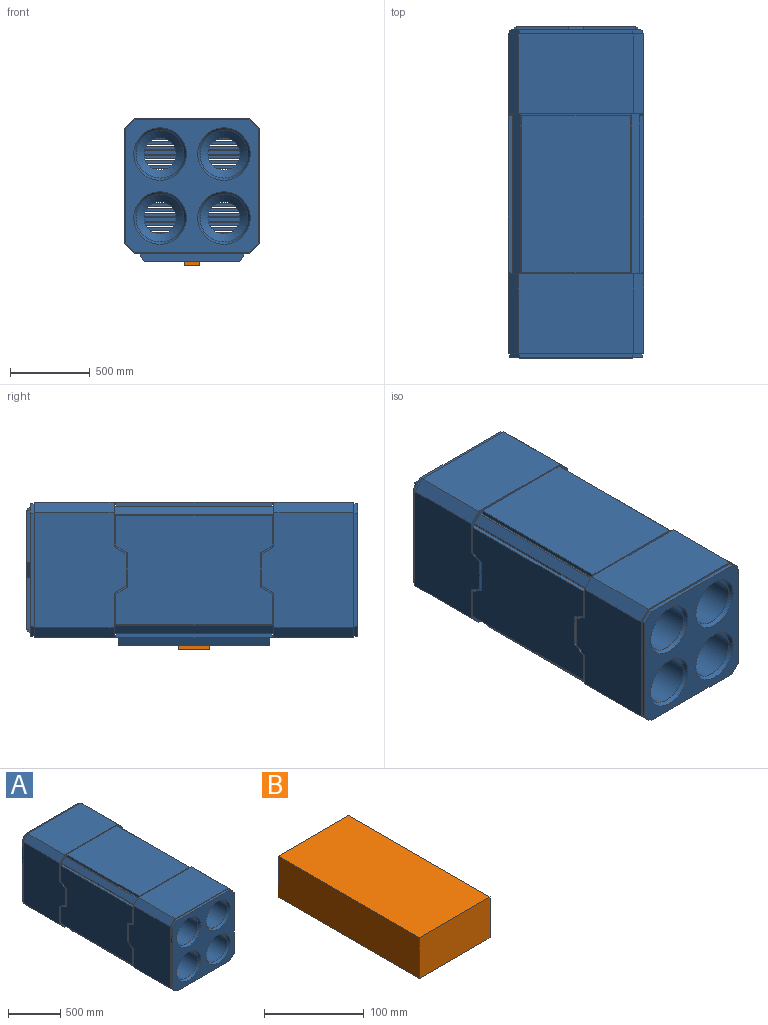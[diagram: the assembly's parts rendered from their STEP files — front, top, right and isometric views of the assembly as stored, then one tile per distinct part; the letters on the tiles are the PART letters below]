
ASSEMBLY  parts=2 mates=1
PART A: 237 faces, bbox 850x2075x900 mm
  f0: plane 950x600mm, normal (0,0,-1), area 550000mm2, adj f155,f156,f157,f231,f232,f233,f234,f235
  f1: plane 980x680mm, normal (0,0,-1), area 41551.7mm2, adj f32,f33,f34,f155,f156,f157,f171,f231
  f2: plane 850x280.77mm, normal (0,-1,0), area 32359.7mm2, adj f4,f13,f15,f22,f23,f24,f141,f158
  f3: plane 850x280.77mm, normal (0,1,0), area 32359.7mm2, adj f4,f12,f14,f16,f17,f18,f139,f158
  f4: plane 1000x700mm, normal (1,0,0), area 35332.1mm2, adj f2,f3,f5,f6,f14,f15,f21,f27
  f5: plane 190x25mm, normal (0,-1,0), area 4750mm2, adj f4,f7,f37,f136
  f6: plane 190x25mm, normal (0,1,0), area 4750mm2, adj f4,f7,f37,f132
  f7: plane 980x680mm, normal (1,0,0), area 627895.2mm2, adj f5,f6,f35,f36,f37,f38,f132,f133
  f8: plane 830x830mm, normal (0,1,0), area 111488.2mm2, adj f45,f46,f47,f48,f49,f50,f51,f52
  f9: plane 750x750mm, normal (0,1,0), area 394500mm2, adj f50,f51,f52,f53,f54,f55,f56,f57
  f10: plane 850x850mm, normal (0,1,0), area 32153.9mm2, adj f22,f23,f24,f25,f26,f45,f46,f47
  f11: plane 850x850mm, normal (0,-1,0), area 32153.9mm2, adj f16,f17,f18,f19,f20,f39,f40,f41
  f12: plane 1000x700mm, normal (0,0,-1), area 33600mm2, adj f3,f14,f27,f32,f33,f34,f162,f171
  f13: plane 1000x700mm, normal (0,0,1), area 33600mm2, adj f2,f15,f21,f28,f29,f30,f163,f170
  f14: plane 1000x50mm, normal (0.71,0,-0.71), area 70710.7mm2, adj f3,f4,f12,f27
  f15: plane 1000x50mm, normal (0.71,0,0.71), area 70710.7mm2, adj f2,f4,f13,f21
  f16: plane 720.71x500mm, normal (0,0,-1), area 360355.3mm2, adj f3,f11,f17,f164
  f17: plane 500x64.64mm, normal (0.71,0,-0.71), area 45710.7mm2, adj f3,f11,f16,f18
  f18: plane 720.71x575mm, normal (1,0,0), area 378741.7mm2, adj f3,f11,f17,f19,f21,f138,f139,f140
  f19: plane 500x64.64mm, normal (0.71,0,0.71), area 45710.7mm2, adj f11,f18,f20,f21
  f20: plane 720.71x500mm, normal (0,0,1), area 360355.3mm2, adj f11,f19,f21,f166
  f21: plane 850x280.77mm, normal (0,1,0), area 32359.7mm2, adj f4,f13,f15,f18,f19,f20,f138,f158
  f22: plane 720.71x500mm, normal (0,0,1), area 360355.3mm2, adj f2,f10,f23,f167
  f23: plane 500x64.64mm, normal (0.71,0,0.71), area 45710.7mm2, adj f2,f10,f22,f24
  f24: plane 720.71x575mm, normal (1,0,0), area 378741.7mm2, adj f2,f10,f23,f25,f27,f141,f142,f143
  f25: plane 500x64.64mm, normal (0.71,0,-0.71), area 45710.7mm2, adj f10,f24,f26,f27
  f26: plane 720.71x500mm, normal (0,0,-1), area 360355.3mm2, adj f10,f25,f27,f169
  f27: plane 850x280.77mm, normal (0,-1,0), area 32359.7mm2, adj f4,f12,f14,f24,f25,f26,f143,f158
  f28: plane 680x25mm, normal (0,1,0), area 17000mm2, adj f13,f30,f31,f170
  f29: plane 680x25mm, normal (0,-1,0), area 17000mm2, adj f13,f30,f31,f170
  f30: plane 980x25mm, normal (1,0,0), area 24500mm2, adj f13,f28,f29,f31
  f31: plane 980x680mm, normal (0,0,1), area 666400mm2, adj f28,f29,f30,f170
  f32: plane 680x25mm, normal (0,-1,0), area 17000mm2, adj f1,f12,f34,f171
  f33: plane 680x25mm, normal (0,1,0), area 17000mm2, adj f1,f12,f34,f171
  f34: plane 980x25mm, normal (1,0,0), area 24500mm2, adj f1,f12,f32,f33
  f35: plane 980x25mm, normal (0,0,1), area 24500mm2, adj f4,f7,f36,f38
  f36: plane 190x25mm, normal (0,-1,0), area 4750mm2, adj f4,f7,f35,f135
  f37: plane 980x25mm, normal (0,0,-1), area 24500mm2, adj f4,f5,f6,f7
  f38: plane 190x25mm, normal (0,1,0), area 4750mm2, adj f4,f7,f35,f133
  f39: plane 712.43x25mm, normal (0,0,1), area 17810.7mm2, adj f11,f43,f44,f178
  f40: plane 712.43x25mm, normal (0,0,-1), area 17810.7mm2, adj f11,f41,f44,f176
  f41: plane 58.79x58.79mm, normal (0.71,0,-0.71), area 2078.4mm2, adj f11,f40,f42,f44
  f42: plane 712.43x25mm, normal (1,0,0), area 17810.7mm2, adj f11,f41,f43,f44
  f43: plane 58.79x58.79mm, normal (0.71,0,0.71), area 2078.4mm2, adj f11,f39,f42,f44
  f44: plane 830x830mm, normal (0,-1,0), area 342212.9mm2, adj f39,f40,f41,f42,f43,f146,f147,f176
  f45: plane 712.43x25mm, normal (0,0,1), area 17810.7mm2, adj f8,f10,f46,f179
  f46: plane 58.79x58.79mm, normal (0.71,0,0.71), area 2078.4mm2, adj f8,f10,f45,f47
  f47: plane 712.43x25mm, normal (1,0,0), area 17810.7mm2, adj f8,f10,f46,f48
  f48: plane 58.79x58.79mm, normal (0.71,0,-0.71), area 2078.4mm2, adj f8,f10,f47,f49
  f49: plane 712.43x25mm, normal (0,0,-1), area 17810.7mm2, adj f8,f10,f48,f181
  f50: plane 750x25mm, normal (0,0,-1), area 16750mm2, adj f8,f9,f52,f128,f131,f182,f210
  f51: plane 750x25mm, normal (0,0,1), area 16750mm2, adj f8,f9,f52,f125,f129,f182,f207
  f52: plane 750x25mm, normal (1,0,0), area 16750mm2, adj f8,f9,f50,f51,f126,f127,f130
  f53: plane 700x25mm, normal (0,0,1), area 17500mm2, adj f9,f55,f154,f183
  f54: plane 700x25mm, normal (0,0,-1), area 17500mm2, adj f9,f55,f154,f183
  f55: plane 25x10mm, normal (-1,0,0), area 250mm2, adj f9,f53,f54,f154
  f56: plane 700x25mm, normal (0,0,1), area 17500mm2, adj f9,f58,f154,f184
  f57: plane 700x25mm, normal (0,0,-1), area 17500mm2, adj f9,f58,f154,f184
  f58: plane 25x10mm, normal (-1,0,0), area 250mm2, adj f9,f56,f57,f154
  f59: plane 700x25mm, normal (0,0,1), area 17500mm2, adj f9,f61,f154,f185
  f60: plane 700x25mm, normal (0,0,-1), area 17500mm2, adj f9,f61,f154,f185
  f61: plane 25x10mm, normal (-1,0,0), area 250mm2, adj f9,f59,f60,f154
  f62: plane 700x25mm, normal (0,0,1), area 17500mm2, adj f9,f64,f154,f186
  f63: plane 700x25mm, normal (0,0,-1), area 17500mm2, adj f9,f64,f154,f186
  f64: plane 25x10mm, normal (-1,0,0), area 250mm2, adj f9,f62,f63,f154
  f65: plane 700x25mm, normal (0,0,1), area 17500mm2, adj f9,f67,f154,f187
  f66: plane 700x25mm, normal (0,0,-1), area 17500mm2, adj f9,f67,f154,f187
  f67: plane 25x10mm, normal (-1,0,0), area 250mm2, adj f9,f65,f66,f154
  f68: plane 700x25mm, normal (0,0,1), area 17500mm2, adj f9,f70,f154,f188
  f69: plane 700x25mm, normal (0,0,-1), area 17500mm2, adj f9,f70,f154,f188
  f70: plane 25x10mm, normal (-1,0,0), area 250mm2, adj f9,f68,f69,f154
  f71: plane 700x25mm, normal (0,0,1), area 17500mm2, adj f9,f73,f154,f189
  f72: plane 700x25mm, normal (0,0,-1), area 17500mm2, adj f9,f73,f154,f189
  f73: plane 25x10mm, normal (-1,0,0), area 250mm2, adj f9,f71,f72,f154
  f74: plane 700x25mm, normal (0,0,1), area 17500mm2, adj f9,f76,f154,f190
  f75: plane 700x25mm, normal (0,0,-1), area 17500mm2, adj f9,f76,f154,f190
  f76: plane 25x10mm, normal (-1,0,0), area 250mm2, adj f9,f74,f75,f154
  f77: plane 700x25mm, normal (0,0,1), area 17500mm2, adj f9,f79,f154,f191
  f78: plane 700x25mm, normal (0,0,-1), area 17500mm2, adj f9,f79,f154,f191
  f79: plane 25x10mm, normal (-1,0,0), area 250mm2, adj f9,f77,f78,f154
  f80: plane 700x25mm, normal (0,0,1), area 17500mm2, adj f9,f82,f154,f192
  f81: plane 700x25mm, normal (0,0,-1), area 17500mm2, adj f9,f82,f154,f192
  f82: plane 25x10mm, normal (-1,0,0), area 250mm2, adj f9,f80,f81,f154
  f83: plane 700x25mm, normal (0,0,1), area 17500mm2, adj f9,f85,f154,f193
  f84: plane 700x25mm, normal (0,0,-1), area 17500mm2, adj f9,f85,f154,f193
  f85: plane 25x10mm, normal (-1,0,0), area 250mm2, adj f9,f83,f84,f154
  f86: plane 700x25mm, normal (0,0,1), area 17500mm2, adj f9,f88,f154,f194
  f87: plane 700x25mm, normal (0,0,-1), area 17500mm2, adj f9,f88,f154,f194
  f88: plane 25x10mm, normal (-1,0,0), area 250mm2, adj f9,f86,f87,f154
  f89: plane 700x25mm, normal (0,0,1), area 17500mm2, adj f9,f91,f154,f195
  f90: plane 700x25mm, normal (0,0,-1), area 17500mm2, adj f9,f91,f154,f195
  f91: plane 25x10mm, normal (-1,0,0), area 250mm2, adj f9,f89,f90,f154
  f92: plane 700x25mm, normal (0,0,1), area 17500mm2, adj f9,f94,f154,f196
  f93: plane 700x25mm, normal (0,0,-1), area 17500mm2, adj f9,f94,f154,f196
  f94: plane 25x10mm, normal (-1,0,0), area 250mm2, adj f9,f92,f93,f154
  f95: plane 700x25mm, normal (0,0,1), area 17500mm2, adj f9,f97,f154,f197
  f96: plane 700x25mm, normal (0,0,-1), area 17500mm2, adj f9,f97,f154,f197
  f97: plane 25x10mm, normal (-1,0,0), area 250mm2, adj f9,f95,f96,f154
  f98: plane 700x25mm, normal (0,0,1), area 17500mm2, adj f9,f100,f154,f198
  f99: plane 700x25mm, normal (0,0,-1), area 17500mm2, adj f9,f100,f154,f198
  f100: plane 25x10mm, normal (-1,0,0), area 250mm2, adj f9,f98,f99,f154
  f101: plane 700x25mm, normal (0,0,1), area 17500mm2, adj f9,f103,f154,f199
  f102: plane 700x25mm, normal (0,0,-1), area 17500mm2, adj f9,f103,f154,f199
  f103: plane 25x10mm, normal (-1,0,0), area 250mm2, adj f9,f101,f102,f154
  f104: plane 700x25mm, normal (0,0,1), area 17500mm2, adj f9,f106,f154,f200
  f105: plane 700x25mm, normal (0,0,-1), area 17500mm2, adj f9,f106,f154,f200
  f106: plane 25x10mm, normal (-1,0,0), area 250mm2, adj f9,f104,f105,f154
  f107: plane 700x25mm, normal (0,0,1), area 17500mm2, adj f9,f109,f154,f201
  f108: plane 700x25mm, normal (0,0,-1), area 17500mm2, adj f9,f109,f154,f201
  f109: plane 25x10mm, normal (-1,0,0), area 250mm2, adj f9,f107,f108,f154
  f110: plane 700x25mm, normal (0,0,1), area 17500mm2, adj f9,f112,f154,f202
  f111: plane 700x25mm, normal (0,0,-1), area 17500mm2, adj f9,f112,f154,f202
  f112: plane 25x10mm, normal (-1,0,0), area 250mm2, adj f9,f110,f111,f154
  f113: plane 700x25mm, normal (0,0,1), area 17500mm2, adj f9,f115,f154,f203
  f114: plane 700x25mm, normal (0,0,-1), area 17500mm2, adj f9,f115,f154,f203
  f115: plane 25x10mm, normal (-1,0,0), area 250mm2, adj f9,f113,f114,f154
  f116: plane 700x25mm, normal (0,0,1), area 17500mm2, adj f9,f118,f154,f204
  f117: plane 700x25mm, normal (0,0,-1), area 17500mm2, adj f9,f118,f154,f204
  f118: plane 25x10mm, normal (-1,0,0), area 250mm2, adj f9,f116,f117,f154
  f119: plane 700x25mm, normal (0,0,1), area 17500mm2, adj f9,f121,f154,f205
  f120: plane 700x25mm, normal (0,0,-1), area 17500mm2, adj f9,f121,f154,f205
  f121: plane 25x10mm, normal (-1,0,0), area 250mm2, adj f9,f119,f120,f154
  f122: plane 700x25mm, normal (0,0,1), area 17500mm2, adj f9,f124,f154,f206
  f123: plane 700x25mm, normal (0,0,-1), area 17500mm2, adj f9,f124,f154,f206
  f124: plane 25x10mm, normal (-1,0,0), area 250mm2, adj f9,f122,f123,f154
  f125: plane 20x20mm, normal (1,0,0), area 200mm2, adj f8,f51,f129
  f126: plane 20x20mm, normal (0,0,1), area 200mm2, adj f8,f52,f130
  f127: plane 20x20mm, normal (0,0,-1), area 200mm2, adj f8,f52,f130
  f128: plane 20x20mm, normal (1,0,0), area 200mm2, adj f8,f50,f131
  f129: plane 100x20mm, normal (0,0.71,0.71), area 2828.4mm2, adj f8,f51,f125,f207
  f130: plane 100x20mm, normal (0.71,0.71,0), area 2828.4mm2, adj f8,f52,f126,f127
  f131: plane 100x20mm, normal (0,0.71,-0.71), area 2828.4mm2, adj f8,f50,f128,f210
  f132: plane 75x43.3mm, normal (0,0.5,0.87), area 2165.1mm2, adj f4,f6,f7,f134
  f133: plane 75x43.3mm, normal (0,0.5,-0.87), area 2165.1mm2, adj f4,f7,f38,f134
  f134: plane 213.4x25mm, normal (0,1,0), area 5334.9mm2, adj f4,f7,f132,f133
  f135: plane 75x43.3mm, normal (0,-0.5,-0.87), area 2165.1mm2, adj f4,f7,f36,f137
  f136: plane 75x43.3mm, normal (0,-0.5,0.87), area 2165.1mm2, adj f4,f5,f7,f137
  f137: plane 213.4x25mm, normal (0,-1,0), area 5334.9mm2, adj f4,f7,f135,f136
  f138: plane 75x43.3mm, normal (0,0.5,0.87), area 2165.1mm2, adj f4,f18,f21,f140
  f139: plane 75x43.3mm, normal (0,0.5,-0.87), area 2165.1mm2, adj f3,f4,f18,f140
  f140: plane 201.85x25mm, normal (0,1,0), area 5046.3mm2, adj f4,f18,f138,f139
  f141: plane 75x43.3mm, normal (0,-0.5,0.87), area 2165.1mm2, adj f2,f4,f24,f142
  f142: plane 201.85x25mm, normal (0,-1,0), area 5046.3mm2, adj f4,f24,f141,f143
  f143: plane 75x43.3mm, normal (0,-0.5,-0.87), area 2165.1mm2, adj f4,f24,f27,f142
  f144: cylinder r=150mm len=1925mm, axis (0,-1,0), area 1814269.8mm2, adj f146,f148
  f145: cylinder r=150mm len=1925mm, axis (0,-1,0), area 1814269.8mm2, adj f147,f149
  f146: cone r=150mm half-angle=30deg, axis (0,-1,0), area 28516mm2, adj f44,f144
  f147: cone r=150mm half-angle=30deg, axis (0,-1,0), area 28516mm2, adj f44,f145
  f148: cone r=100mm half-angle=45deg, axis (0,-1,0), area 55536mm2, adj f144,f150
  f149: cone r=100mm half-angle=45deg, axis (0,-1,0), area 55536mm2, adj f145,f150
  f150: plane 720x720mm, normal (0,1,0), area 392736.3mm2, adj f148,f149,f151,f152,f153,f228,f229,f230
  f151: plane 720x50mm, normal (0,0,-1), area 36000mm2, adj f150,f152,f154,f230
  f152: plane 720x50mm, normal (-1,0,0), area 36000mm2, adj f150,f151,f153,f154
  f153: plane 720x50mm, normal (0,0,1), area 36000mm2, adj f150,f152,f154,f230
  f154: plane 720x720mm, normal (0,-1,0), area 350400mm2, adj f53,f54,f55,f56,f57,f58,f59,f60
  f155: plane 657.74x50mm, normal (0,-1,0), area 31443.4mm2, adj f0,f1,f157,f231
  f156: plane 657.74x50mm, normal (0,1,0), area 31443.4mm2, adj f0,f1,f157,f231
  f157: plane 950x50mm, normal (0.87,0,-0.5), area 54848.3mm2, adj f0,f1,f155,f156
  f158: plane 1000x700mm, normal (-1,0,0), area 35332.1mm2, adj f2,f3,f21,f27,f159,f160,f162,f163
  f159: plane 190x25mm, normal (0,-1,0), area 4750mm2, adj f158,f161,f174,f216
  f160: plane 190x25mm, normal (0,1,0), area 4750mm2, adj f158,f161,f174,f212
  f161: plane 980x680mm, normal (-1,0,0), area 627895.2mm2, adj f159,f160,f172,f173,f174,f175,f212,f213
  f162: plane 1000x50mm, normal (-0.71,0,-0.71), area 70710.7mm2, adj f3,f12,f27,f158
  f163: plane 1000x50mm, normal (-0.71,0,0.71), area 70710.7mm2, adj f2,f13,f21,f158
  f164: plane 500x64.64mm, normal (-0.71,0,-0.71), area 45710.7mm2, adj f3,f11,f16,f165
  f165: plane 720.71x575mm, normal (-1,0,0), area 378741.7mm2, adj f3,f11,f21,f164,f166,f218,f219,f220
  f166: plane 500x64.64mm, normal (-0.71,0,0.71), area 45710.7mm2, adj f11,f20,f21,f165
  f167: plane 500x64.64mm, normal (-0.71,0,0.71), area 45710.7mm2, adj f2,f10,f22,f168
  f168: plane 720.71x575mm, normal (-1,0,0), area 378741.7mm2, adj f2,f10,f27,f167,f169,f221,f222,f223
  f169: plane 500x64.64mm, normal (-0.71,0,-0.71), area 45710.7mm2, adj f10,f26,f27,f168
  f170: plane 980x25mm, normal (-1,0,0), area 24500mm2, adj f13,f28,f29,f31
  f171: plane 980x25mm, normal (-1,0,0), area 24500mm2, adj f1,f12,f32,f33
  f172: plane 980x25mm, normal (0,0,1), area 24500mm2, adj f158,f161,f173,f175
  f173: plane 190x25mm, normal (0,-1,0), area 4750mm2, adj f158,f161,f172,f215
  f174: plane 980x25mm, normal (0,0,-1), area 24500mm2, adj f158,f159,f160,f161
  f175: plane 190x25mm, normal (0,1,0), area 4750mm2, adj f158,f161,f172,f213
  f176: plane 58.79x58.79mm, normal (-0.71,0,-0.71), area 2078.4mm2, adj f11,f40,f44,f177
  f177: plane 712.43x25mm, normal (-1,0,0), area 17810.7mm2, adj f11,f44,f176,f178
  f178: plane 58.79x58.79mm, normal (-0.71,0,0.71), area 2078.4mm2, adj f11,f39,f44,f177
  f179: plane 58.79x58.79mm, normal (-0.71,0,0.71), area 2078.4mm2, adj f8,f10,f45,f180
  f180: plane 712.43x25mm, normal (-1,0,0), area 17810.7mm2, adj f8,f10,f179,f181
  f181: plane 58.79x58.79mm, normal (-0.71,0,-0.71), area 2078.4mm2, adj f8,f10,f49,f180
  f182: plane 750x25mm, normal (-1,0,0), area 16750mm2, adj f8,f9,f50,f51,f208,f209,f211
  f183: plane 25x10mm, normal (1,0,0), area 250mm2, adj f9,f53,f54,f154
  f184: plane 25x10mm, normal (1,0,0), area 250mm2, adj f9,f56,f57,f154
  f185: plane 25x10mm, normal (1,0,0), area 250mm2, adj f9,f59,f60,f154
  f186: plane 25x10mm, normal (1,0,0), area 250mm2, adj f9,f62,f63,f154
  f187: plane 25x10mm, normal (1,0,0), area 250mm2, adj f9,f65,f66,f154
  f188: plane 25x10mm, normal (1,0,0), area 250mm2, adj f9,f68,f69,f154
  f189: plane 25x10mm, normal (1,0,0), area 250mm2, adj f9,f71,f72,f154
  f190: plane 25x10mm, normal (1,0,0), area 250mm2, adj f9,f74,f75,f154
  f191: plane 25x10mm, normal (1,0,0), area 250mm2, adj f9,f77,f78,f154
  f192: plane 25x10mm, normal (1,0,0), area 250mm2, adj f9,f80,f81,f154
  f193: plane 25x10mm, normal (1,0,0), area 250mm2, adj f9,f83,f84,f154
  f194: plane 25x10mm, normal (1,0,0), area 250mm2, adj f9,f86,f87,f154
  f195: plane 25x10mm, normal (1,0,0), area 250mm2, adj f9,f89,f90,f154
  f196: plane 25x10mm, normal (1,0,0), area 250mm2, adj f9,f92,f93,f154
  f197: plane 25x10mm, normal (1,0,0), area 250mm2, adj f9,f95,f96,f154
  f198: plane 25x10mm, normal (1,0,0), area 250mm2, adj f9,f98,f99,f154
  f199: plane 25x10mm, normal (1,0,0), area 250mm2, adj f9,f101,f102,f154
  f200: plane 25x10mm, normal (1,0,0), area 250mm2, adj f9,f104,f105,f154
  f201: plane 25x10mm, normal (1,0,0), area 250mm2, adj f9,f107,f108,f154
  f202: plane 25x10mm, normal (1,0,0), area 250mm2, adj f9,f110,f111,f154
  f203: plane 25x10mm, normal (1,0,0), area 250mm2, adj f9,f113,f114,f154
  f204: plane 25x10mm, normal (1,0,0), area 250mm2, adj f9,f116,f117,f154
  f205: plane 25x10mm, normal (1,0,0), area 250mm2, adj f9,f119,f120,f154
  f206: plane 25x10mm, normal (1,0,0), area 250mm2, adj f9,f122,f123,f154
  f207: plane 20x20mm, normal (-1,0,0), area 200mm2, adj f8,f51,f129
  f208: plane 20x20mm, normal (0,0,1), area 200mm2, adj f8,f182,f211
  f209: plane 20x20mm, normal (0,0,-1), area 200mm2, adj f8,f182,f211
  f210: plane 20x20mm, normal (-1,0,0), area 200mm2, adj f8,f50,f131
  f211: plane 100x20mm, normal (-0.71,0.71,0), area 2828.4mm2, adj f8,f182,f208,f209
  f212: plane 75x43.3mm, normal (0,0.5,0.87), area 2165.1mm2, adj f158,f160,f161,f214
  f213: plane 75x43.3mm, normal (0,0.5,-0.87), area 2165.1mm2, adj f158,f161,f175,f214
  f214: plane 213.4x25mm, normal (0,1,0), area 5334.9mm2, adj f158,f161,f212,f213
  f215: plane 75x43.3mm, normal (0,-0.5,-0.87), area 2165.1mm2, adj f158,f161,f173,f217
  f216: plane 75x43.3mm, normal (0,-0.5,0.87), area 2165.1mm2, adj f158,f159,f161,f217
  f217: plane 213.4x25mm, normal (0,-1,0), area 5334.9mm2, adj f158,f161,f215,f216
  f218: plane 75x43.3mm, normal (0,0.5,0.87), area 2165.1mm2, adj f21,f158,f165,f220
  f219: plane 75x43.3mm, normal (0,0.5,-0.87), area 2165.1mm2, adj f3,f158,f165,f220
  f220: plane 201.85x25mm, normal (0,1,0), area 5046.3mm2, adj f158,f165,f218,f219
  f221: plane 75x43.3mm, normal (0,-0.5,0.87), area 2165.1mm2, adj f2,f158,f168,f222
  f222: plane 201.85x25mm, normal (0,-1,0), area 5046.3mm2, adj f158,f168,f221,f223
  f223: plane 75x43.3mm, normal (0,-0.5,-0.87), area 2165.1mm2, adj f27,f158,f168,f222
  f224: cylinder r=150mm len=1925mm, axis (0,-1,0), area 1814269.8mm2, adj f226,f228
  f225: cylinder r=150mm len=1925mm, axis (0,-1,0), area 1814269.8mm2, adj f227,f229
  f226: cone r=150mm half-angle=30deg, axis (0,-1,0), area 28516mm2, adj f44,f224
  f227: cone r=150mm half-angle=30deg, axis (0,-1,0), area 28516mm2, adj f44,f225
  f228: cone r=100mm half-angle=45deg, axis (0,-1,0), area 55536mm2, adj f150,f224
  f229: cone r=100mm half-angle=45deg, axis (0,-1,0), area 55536mm2, adj f150,f225
  f230: plane 720x50mm, normal (1,0,0), area 36000mm2, adj f150,f151,f153,f154
  f231: plane 950x50mm, normal (-0.87,0,-0.5), area 54848.3mm2, adj f0,f1,f155,f156
  f232: plane 100x25mm, normal (0,1,0), area 2500mm2, adj f0,f233,f235,f236
  f233: plane 200x25mm, normal (1,0,0), area 5000mm2, adj f0,f232,f234,f236
  f234: plane 100x25mm, normal (0,-1,0), area 2500mm2, adj f0,f233,f235,f236
  f235: plane 200x25mm, normal (-1,0,0), area 5000mm2, adj f0,f232,f234,f236
  f236: plane 200x100mm, normal (0,0,-1), area 20000mm2, adj f232,f233,f234,f235
PART B: 6 faces, bbox 100x200x50 mm
  f0: plane 100x50mm, normal (0,-1,0), area 5000mm2, adj f1,f3,f4,f5
  f1: plane 200x50mm, normal (-1,0,0), area 10000mm2, adj f0,f2,f4,f5
  f2: plane 100x50mm, normal (0,1,0), area 5000mm2, adj f1,f3,f4,f5
  f3: plane 200x50mm, normal (1,0,0), area 10000mm2, adj f0,f2,f4,f5
  f4: plane 200x100mm, normal (0,0,-1), area 20000mm2, adj f0,f1,f2,f3
  f5: plane 200x100mm, normal (0,0,1), area 20000mm2, adj f0,f1,f2,f3
PLACE A t=(-14.65,-1012.5,90.85)mm
PLACE B t=(-14.65,-1012.5,90.85)mm
MATE fastened B.f5 <-> A.f236  axis (0,0,1) through (-14.65,-12.5,40.85)mm
